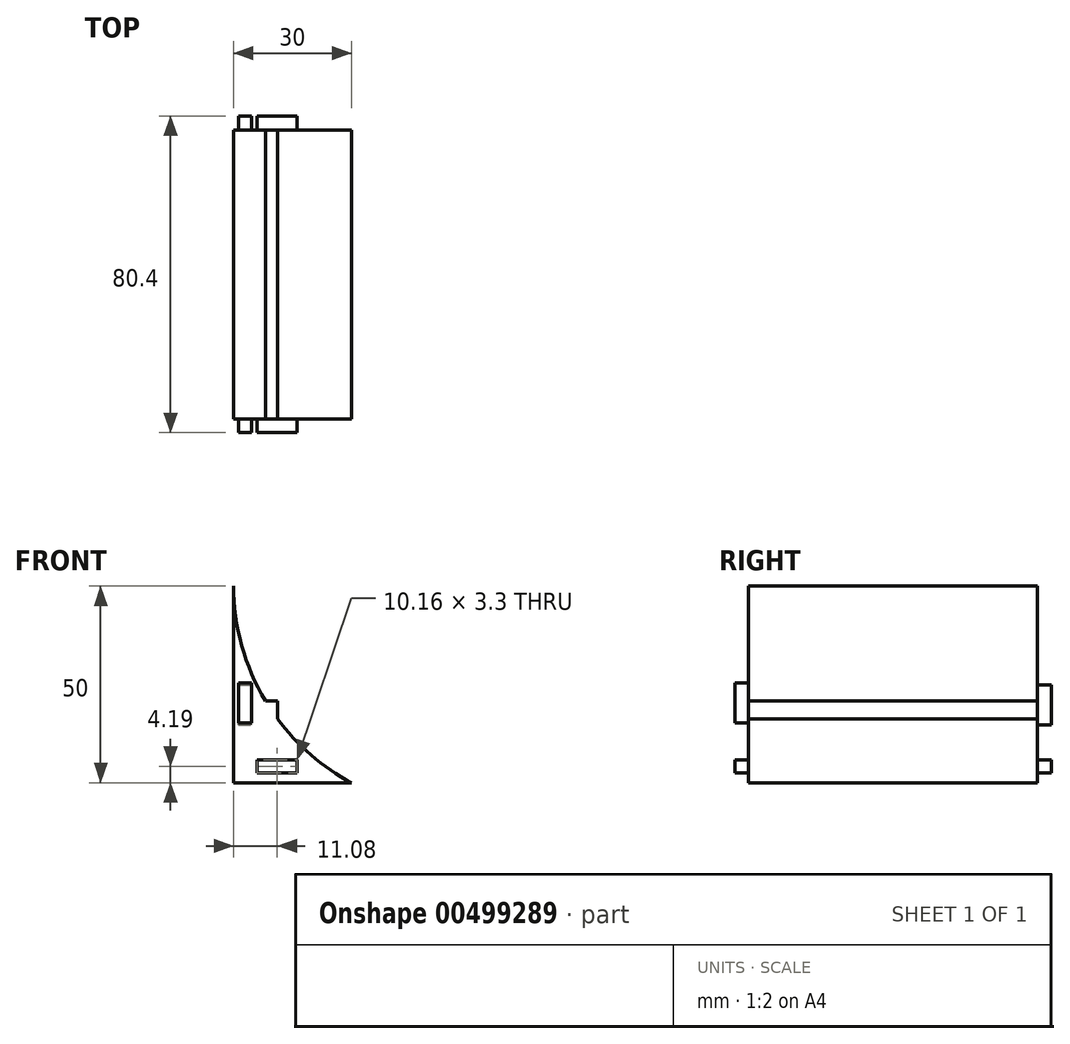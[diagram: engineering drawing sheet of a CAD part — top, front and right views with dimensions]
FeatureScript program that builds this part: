
annotation { "Feature Type Name" : "Feature", "Feature Type Description" : "" }
export const myFeature = defineFeature(function(context is Context, id is Id, definition is map)
    precondition{}
    {
        {
            var Q0;
            Q0=qCreatedBy(makeId("Front.planeOp"),FACE);
            var sketch = newSketch(context, id + "F0", { "sketchPlane" : qUnion([Q0])});
            skLineSegment(sketch, "E0", {"start": v(0, 0) * mm, "end": v(30, 0) * mm});
            skLineSegment(sketch, "E1", {"start": v(0, 0) * mm, "end": v(0, 50) * mm});
            skLineSegment(sketch, "E2", {"start": v(0, 50) * mm, "end": v(30, 0) * mm});
            skArc(sketch, "E3", {"start": v(0, 50) * mm, "mid": v(8.08, 20.85) * mm, "end": v(30, 0) * mm});
            skLineSegment(sketch, "E4", {"start": v(0, 0) * mm, "end": v(6, 0) * mm, "construction": true});
            skLineSegment(sketch, "E5", {"start": v(0, 0) * mm, "end": v(0, 2.54) * mm, "construction": true});
            skLineSegment(sketch, "E6", {"start": v(0, 2.54) * mm, "end": v(6, 2.54) * mm, "construction": true});
            skLineSegment(sketch, "E7.bottom", {"start": v(6, 2.54) * mm, "end": v(16.16, 2.54) * mm});
            skLineSegment(sketch, "E7.top", {"start": v(6, 5.84) * mm, "end": v(16.16, 5.84) * mm});
            skLineSegment(sketch, "E7.left", {"start": v(6, 2.54) * mm, "end": v(6, 5.84) * mm});
            skLineSegment(sketch, "E7.right", {"start": v(16.16, 2.54) * mm, "end": v(16.16, 5.84) * mm});
            skLineSegment(sketch, "E8", {"start": v(0, -0.56) * mm, "end": v(0, 14.68) * mm, "construction": true});
            skPoint(sketch, "E8.startSnap0", {"position": v(0, 1.27) * mm});
            skLineSegment(sketch, "E9", {"start": v(0, 14.68) * mm, "end": v(1.27, 14.68) * mm, "construction": true});
            skLineSegment(sketch, "E10.bottom", {"start": v(1.27, 14.68) * mm, "end": v(4.57, 14.68) * mm});
            skLineSegment(sketch, "E10.top", {"start": v(1.27, 24.84) * mm, "end": v(4.57, 24.84) * mm});
            skLineSegment(sketch, "E10.left", {"start": v(1.27, 14.68) * mm, "end": v(1.27, 24.84) * mm});
            skLineSegment(sketch, "E10.right", {"start": v(4.57, 14.68) * mm, "end": v(4.57, 24.84) * mm});
            skSolve(sketch);
        }
        {
            var Q0;
            Q0=makeQuery(id+"F0.imprint","IMPRINT",FACE,{"disambiguationData":[TD([[makeQuery(id+"F0.imprint","IMPRINT",EDGE,{"derivedFrom":sQuery(id+"F0.wireOp",EDGE,"E0")}),1.0]])]});
            var Q1;
            Q1=makeQuery(id+"F0.imprint","IMPRINT",FACE,{"disambiguationData":[TD([[makeQuery(id+"F0.imprint","IMPRINT",EDGE,{"derivedFrom":sQuery(id+"F0.wireOp",EDGE,"E10.bottom")}),1.0]])]});
            var Q2;
            Q2=makeQuery(id+"F0.imprint","IMPRINT",FACE,{"disambiguationData":[TD([[makeQuery(id+"F0.imprint","IMPRINT",EDGE,{"derivedFrom":sQuery(id+"F0.wireOp",EDGE,"E7.bottom")}),1.0]])]});
            extrude(context, id + "F1", {"entities" : qUnion([Q0, Q1, Q2]), "depth" : 73.4 * mm});
        }
        {
            var Q0;
            Q0=makeQuery(id+"F0.imprint","IMPRINT",FACE,{"disambiguationData":[TD([[makeQuery(id+"F0.imprint","IMPRINT",EDGE,{"derivedFrom":sQuery(id+"F0.wireOp",EDGE,"E10.bottom")}),1.0]])]});
            var Q1;
            Q1=makeQuery(id+"F0.imprint","IMPRINT",FACE,{"disambiguationData":[TD([[makeQuery(id+"F0.imprint","IMPRINT",EDGE,{"derivedFrom":sQuery(id+"F0.wireOp",EDGE,"E7.bottom")}),1.0]])]});
            extrude(context, id + "F2", {"entities" : qUnion([Q0, Q1]), "operationType" : NewBodyOperationType.ADD, "oppositeDirection" : true, "depth" : 3.5 * mm});
        }
        {
            var Q0;
            Q0=makeQuery(id+"F1.opExtrude","CAP_FACE",FACE,{"disambiguationData":[OSD([sQuery(id+"F0.wireOp",EDGE,"E0"),sQuery(id+"F0.wireOp",EDGE,"E1"),sQuery(id+"F0.wireOp",EDGE,"E3")])],"isStart":false});
            cPlane(context, id + "F3", {"entities" : qUnion([Q0]), "cplaneType" : CPlaneType.OFFSET, "offset" : 0 * mm, "width" : 150 * mm, "height" : 150 * mm});
        }
        {
            var Q0;
            Q0=qCreatedBy(id+"F3.planeOp",FACE);
            var sketch = newSketch(context, id + "F4", { "sketchPlane" : qUnion([Q0])});
            skLineSegment(sketch, "E11", {"start": v(0, 0) * mm, "end": v(6, 0) * mm, "construction": true});
            skLineSegment(sketch, "E12", {"start": v(6, 0) * mm, "end": v(6, 2.54) * mm, "construction": true});
            skLineSegment(sketch, "E13.bottom", {"start": v(6, 2.54) * mm, "end": v(16.16, 2.54) * mm});
            skLineSegment(sketch, "E13.top", {"start": v(6, 5.84) * mm, "end": v(16.16, 5.84) * mm});
            skLineSegment(sketch, "E13.left", {"start": v(6, 2.54) * mm, "end": v(6, 5.84) * mm});
            skLineSegment(sketch, "E13.right", {"start": v(16.16, 2.54) * mm, "end": v(16.16, 5.84) * mm});
            skLineSegment(sketch, "E14", {"start": v(0, 0) * mm, "end": v(0, 15.24) * mm, "construction": true});
            skLineSegment(sketch, "E15", {"start": v(0, 15.24) * mm, "end": v(1.27, 15.24) * mm, "construction": true});
            skLineSegment(sketch, "E16.bottom", {"start": v(1.27, 15.24) * mm, "end": v(4.57, 15.24) * mm});
            skLineSegment(sketch, "E16.top", {"start": v(1.27, 25.4) * mm, "end": v(4.57, 25.4) * mm});
            skLineSegment(sketch, "E16.left", {"start": v(1.27, 15.24) * mm, "end": v(1.27, 25.4) * mm});
            skLineSegment(sketch, "E16.right", {"start": v(4.57, 15.24) * mm, "end": v(4.57, 25.4) * mm});
            skSolve(sketch);
        }
        {
            var Q0;
            Q0=makeQuery(id+"F4.imprint","IMPRINT",FACE,{"disambiguationData":[TD([[makeQuery(id+"F4.imprint","IMPRINT",EDGE,{"derivedFrom":sQuery(id+"F4.wireOp",EDGE,"E16.bottom")}),1.0]])]});
            var Q1;
            Q1=makeQuery(id+"F4.imprint","IMPRINT",FACE,{"disambiguationData":[TD([[makeQuery(id+"F4.imprint","IMPRINT",EDGE,{"derivedFrom":sQuery(id+"F4.wireOp",EDGE,"E13.bottom")}),1.0]])]});
            extrude(context, id + "F5", {"entities" : qUnion([Q0, Q1]), "operationType" : NewBodyOperationType.ADD, "depth" : 3.5 * mm});
        }
        {
            var Q0;
            Q0=qCreatedBy(id+"F3.planeOp",FACE);
            var sketch = newSketch(context, id + "F6", { "sketchPlane" : qUnion([Q0])});
            skArc(sketch, "E17.0.0", {"start": v(30, 0) * mm, "mid": v(8.08, 20.85) * mm, "end": v(0, 50) * mm});
            skLineSegment(sketch, "E17.0.1", {"start": v(0, 50) * mm, "end": v(0, 0) * mm});
            skLineSegment(sketch, "E17.0.2", {"start": v(0, 0) * mm, "end": v(30, 0) * mm});
            skLineSegment(sketch, "E18.bottom", {"start": v(8.08, 20.85) * mm, "end": v(10.64, 20.85) * mm});
            skLineSegment(sketch, "E19.bottom", {"start": v(8.08, 20.85) * mm, "end": v(11.11, 20.85) * mm});
            skLineSegment(sketch, "E19.top", {"start": v(8.08, 16.3) * mm, "end": v(11.11, 16.3) * mm});
            skLineSegment(sketch, "E19.left", {"start": v(8.08, 20.85) * mm, "end": v(8.08, 16.3) * mm});
            skLineSegment(sketch, "E19.right", {"start": v(11.11, 20.85) * mm, "end": v(11.11, 16.3) * mm});
            skSolve(sketch);
        }
        {
            var Q0;
            {var subQ3=sQuery(id+"F6.wireOp",EDGE,"E19.right");Q0=makeQuery(id+"F6.imprint","IMPRINT",FACE,{"disambiguationData":[TD([[makeQuery(id+"F6.imprint","IMPRINT",EDGE,{"derivedFrom":subQ3}),-1.0]])]});}
            extrude(context, id + "F7", {"entities" : qUnion([Q0]), "operationType" : NewBodyOperationType.ADD, "oppositeDirection" : true, "depth" : 73.4 * mm, "offsetDistance" : 25 * mm});
        }
    });
